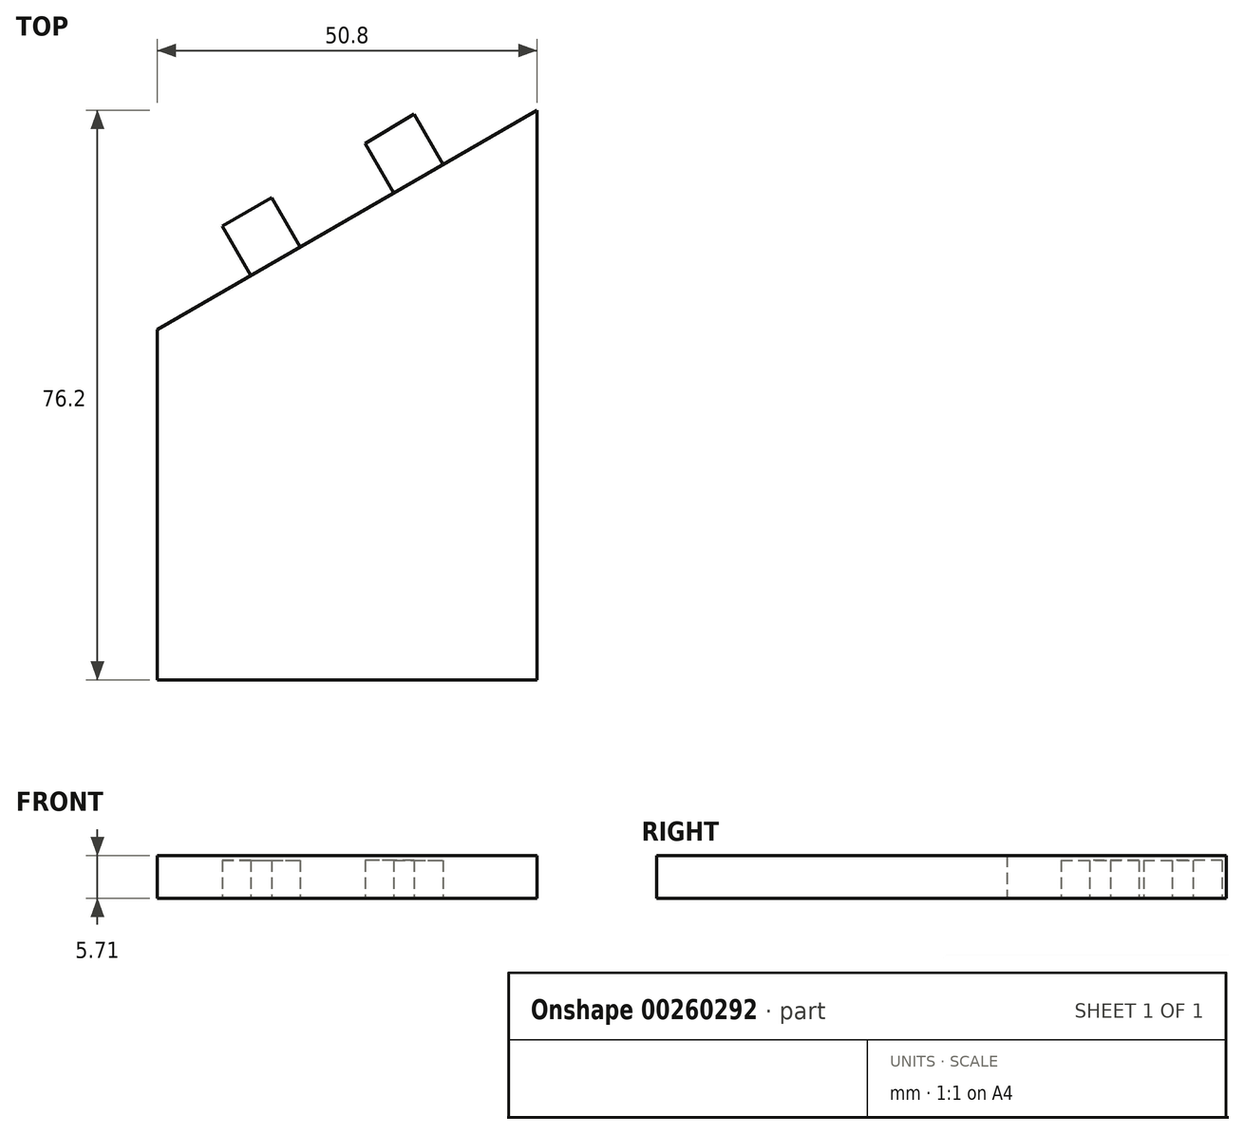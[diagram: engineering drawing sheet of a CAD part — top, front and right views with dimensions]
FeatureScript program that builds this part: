
annotation { "Feature Type Name" : "Feature", "Feature Type Description" : "" }
export const myFeature = defineFeature(function(context is Context, id is Id, definition is map)
    precondition{}
    {
        {
            var Q0;
            Q0=qCreatedBy(makeId("Top.planeOp"),FACE);
            var sketch = newSketch(context, id + "F0", { "sketchPlane" : qUnion([Q0])});
            skLineSegment(sketch, "E0.top", {"start": v(-32.88, -24.4) * mm, "end": v(17.92, -24.4) * mm});
            skLineSegment(sketch, "E0.left", {"start": v(-32.88, 22.47) * mm, "end": v(-32.88, -24.4) * mm});
            skLineSegment(sketch, "E1", {"start": v(-32.88, 22.47) * mm, "end": v(17.92, 51.8) * mm});
            skLineSegment(sketch, "E2", {"start": v(17.92, 51.8) * mm, "end": v(17.92, -24.4) * mm});
            skLineSegment(sketch, "E3", {"start": v(-20.37, 29.7) * mm, "end": v(-24.18, 36.3) * mm});
            skLineSegment(sketch, "E4", {"start": v(-17.58, 40.1) * mm, "end": v(-13.77, 33.5) * mm});
            skLineSegment(sketch, "E5", {"start": v(-1.25, 40.73) * mm, "end": v(-5.06, 47.33) * mm});
            skLineSegment(sketch, "E6", {"start": v(1.47, 51.26) * mm, "end": v(5.35, 44.54) * mm});
            skLineSegment(sketch, "E7", {"start": v(-32.88, 22.47) * mm, "end": v(-41.9, 38.08) * mm, "construction": true});
            skLineSegment(sketch, "E8", {"start": v(17.92, 51.8) * mm, "end": v(9.98, 65.55) * mm, "construction": true});
            skLineSegment(sketch, "E9", {"start": v(-24.18, 36.3) * mm, "end": v(-17.58, 40.1) * mm});
            skLineSegment(sketch, "E10", {"start": v(1.47, 51.26) * mm, "end": v(-5.06, 47.33) * mm});
            skSolve(sketch);
        }
        {
            var Q0;
            Q0=makeQuery(id+"F0.imprint","IMPRINT",FACE,{"disambiguationData":[TD([[makeQuery(id+"F0.imprint","IMPRINT",EDGE,{"derivedFrom":sQuery(id+"F0.wireOp",EDGE,"E0.top")}),1.0]])]});
            extrude(context, id + "F1", {"entities" : qUnion([Q0]), "depth" : 5.7 * mm});
        }
        {
            var Q0;
            {var subQ0=sQuery(id+"F0.wireOp",EDGE,"E5");Q0=makeQuery(id+"F0.imprint","IMPRINT",FACE,{"disambiguationData":[TD([[makeQuery(id+"F0.imprint","IMPRINT",EDGE,{"derivedFrom":subQ0}),-1.0]])]});}
            var Q1;
            {var subQ0=sQuery(id+"F0.wireOp",EDGE,"E3");Q1=makeQuery(id+"F0.imprint","IMPRINT",FACE,{"disambiguationData":[TD([[makeQuery(id+"F0.imprint","IMPRINT",EDGE,{"derivedFrom":subQ0}),-1.0]])]});}
            extrude(context, id + "F2", {"entities" : qUnion([Q0, Q1]), "operationType" : NewBodyOperationType.ADD, "depth" : 5.08 * mm});
        }
    });
